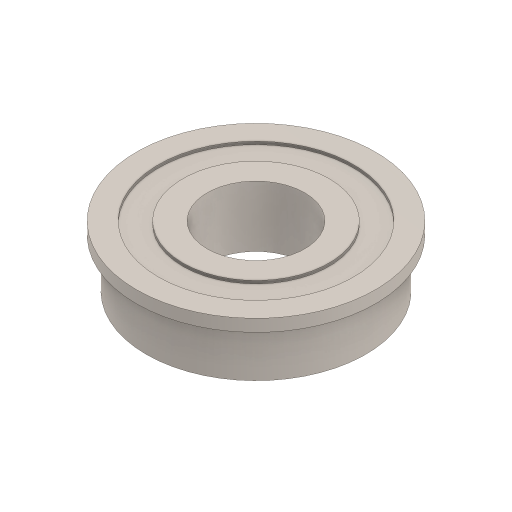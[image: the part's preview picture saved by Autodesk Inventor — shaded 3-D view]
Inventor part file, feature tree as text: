
AUTODESK INVENTOR PART (.ipt)
format: ipt  version: 2024 (Build 280153000, 153)  size: 153,600 bytes
history: native  units: in
note: dims shown in document units (in); Inventor stores cm internally (conversion verified against a paired STEP export)
features: revolve x1
ambient origin geometry x8: Origin, YZ Plane, XZ Plane, XY Plane, X Axis, Y Axis, Z Axis, Center Point
bodies: Solid1 (feature_tree)
feature tree (1):
  revolve  "Revolve1"  [1 undecoded]
note: 1 required parameter value undecoded (feature->parameter linkage not recoverable at this tier; creation-order binding heuristic only, values carry confidence <= 0.55)
